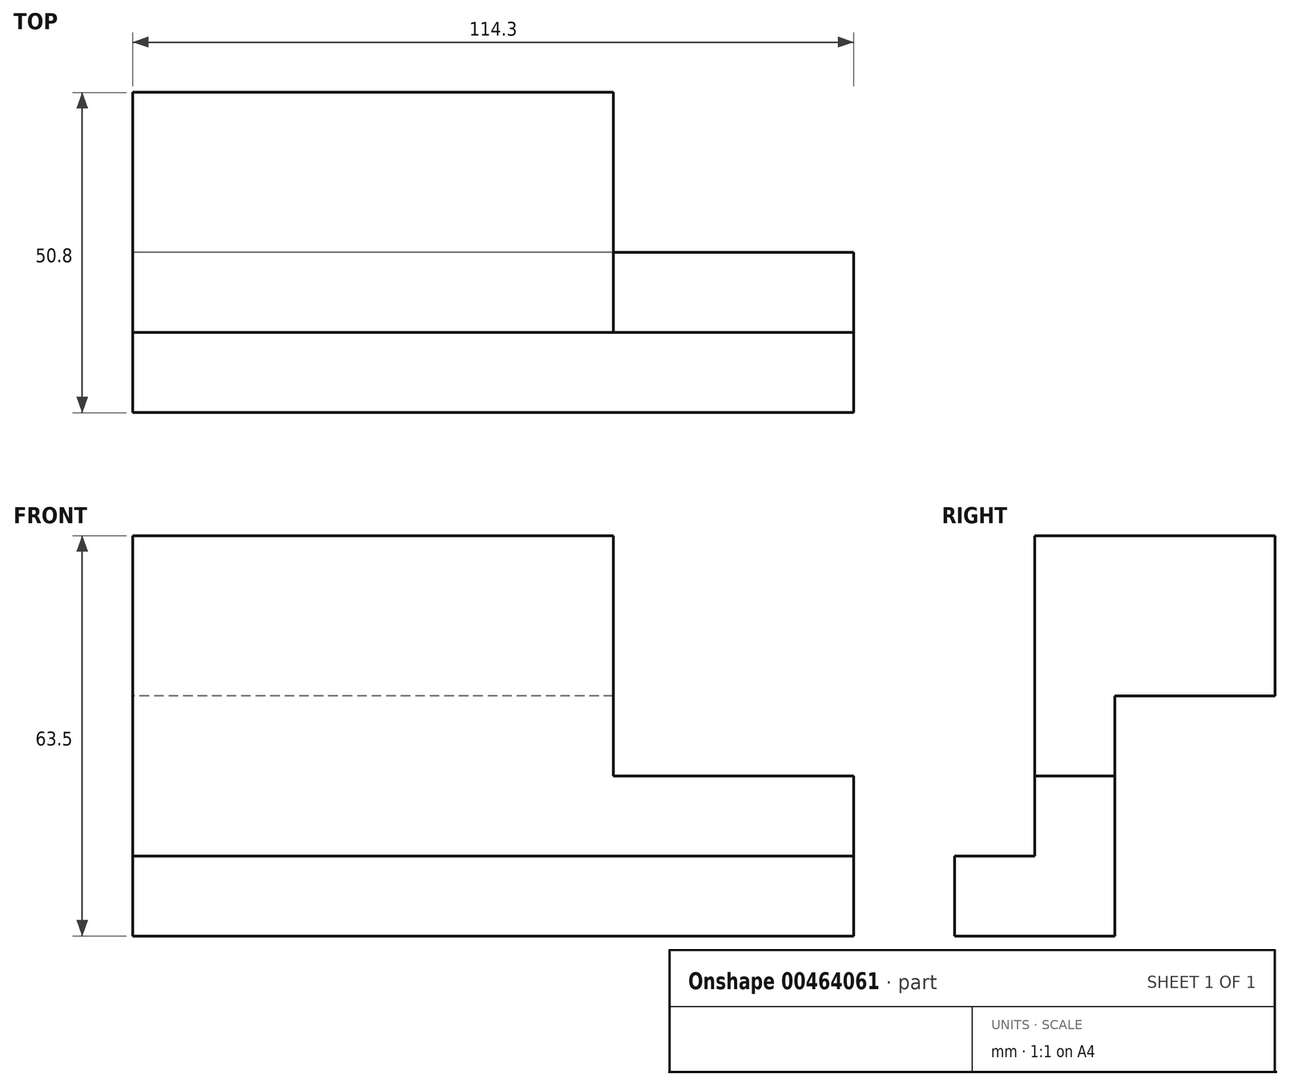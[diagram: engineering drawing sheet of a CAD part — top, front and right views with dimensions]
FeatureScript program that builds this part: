
annotation { "Feature Type Name" : "Feature", "Feature Type Description" : "" }
export const myFeature = defineFeature(function(context is Context, id is Id, definition is map)
    precondition{}
    {
        {
            var Q0;
            Q0=qCreatedBy(makeId("Right.planeOp"),FACE);
            var sketch = newSketch(context, id + "F0", { "sketchPlane" : qUnion([Q0])});
            skLineSegment(sketch, "E0", {"start": v(-39.26, 9.64) * mm, "end": v(-39.26, -3.06) * mm});
            skLineSegment(sketch, "E1", {"start": v(-39.26, -3.06) * mm, "end": v(-13.86, -3.06) * mm});
            skLineSegment(sketch, "E2", {"start": v(-13.86, -3.06) * mm, "end": v(-13.86, 35.04) * mm});
            skLineSegment(sketch, "E3", {"start": v(-13.86, 35.04) * mm, "end": v(11.54, 35.04) * mm});
            skLineSegment(sketch, "E4", {"start": v(11.54, 35.04) * mm, "end": v(11.54, 60.44) * mm});
            skLineSegment(sketch, "E5", {"start": v(11.54, 60.44) * mm, "end": v(-26.56, 60.44) * mm});
            skLineSegment(sketch, "E6", {"start": v(-26.56, 60.44) * mm, "end": v(-26.56, 9.64) * mm});
            skLineSegment(sketch, "E7", {"start": v(-26.56, 9.64) * mm, "end": v(-39.26, 9.64) * mm});
            skLineSegment(sketch, "E8", {"start": v(-26.56, 22.34) * mm, "end": v(-13.86, 22.34) * mm});
            skSolve(sketch);
        }
        {
            var Q0;
            Q0=makeQuery(id+"F0.imprint","IMPRINT",FACE,{"disambiguationData":[TD([[makeQuery(id+"F0.imprint","IMPRINT",EDGE,{"derivedFrom":sQuery(id+"F0.wireOp",EDGE,"E0")}),1.0]])]});
            extrude(context, id + "F1", {"entities" : qUnion([Q0]), "depth" : 114.3 * mm});
        }
        {
            var Q0;
            Q0 = qSketchRegion(id + "F0", true);
            extrude(context, id + "F2", {"entities" : qUnion([Q0]), "operationType" : NewBodyOperationType.ADD, "depth" : 76.2 * mm});
        }
    });
